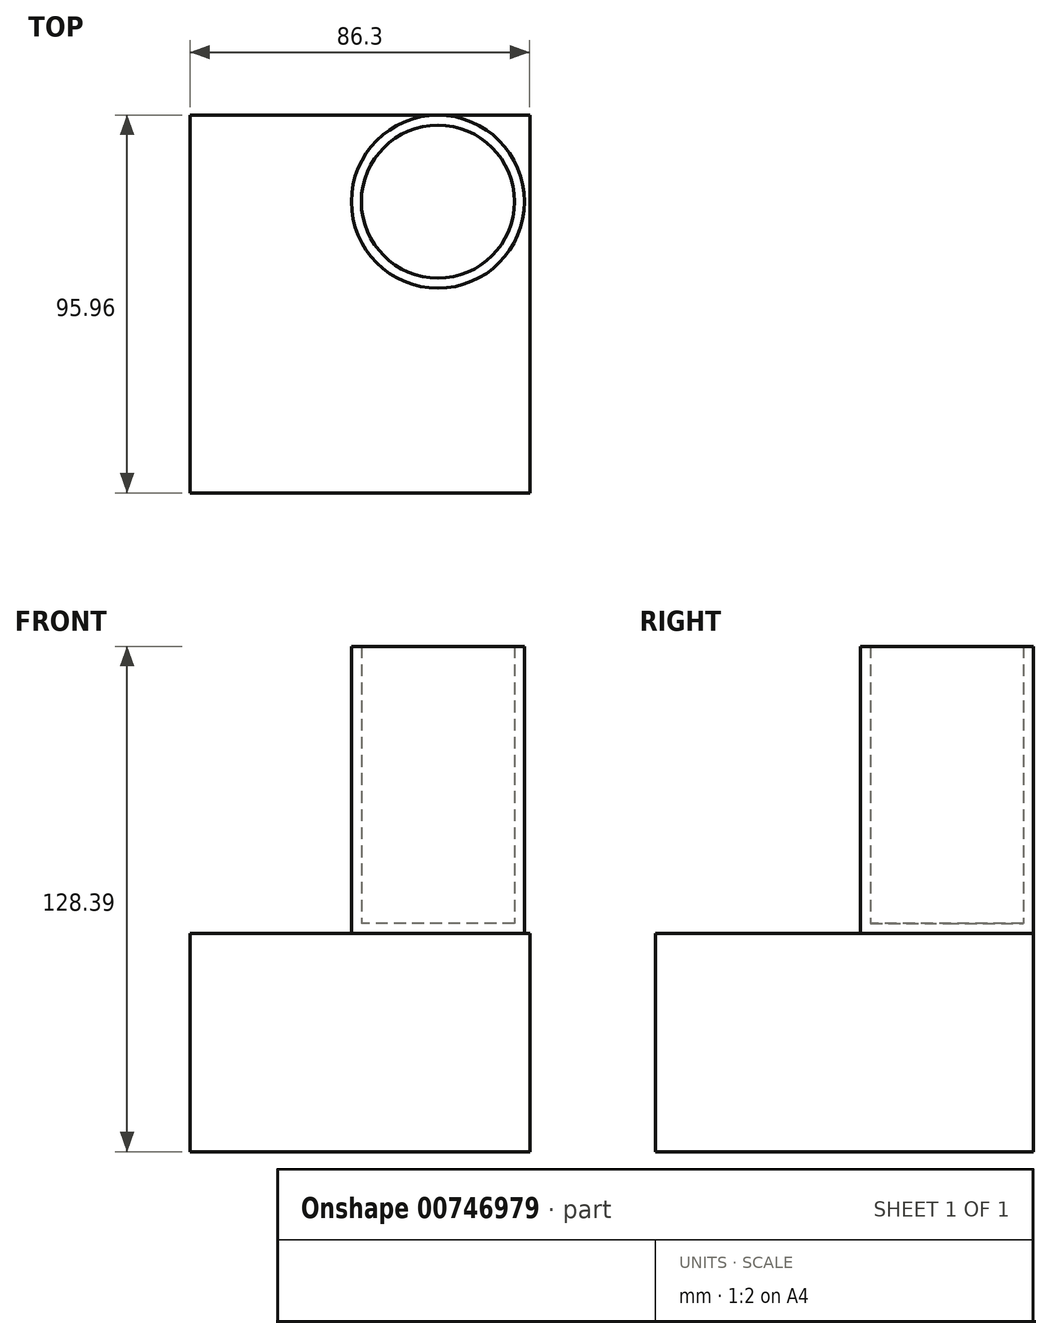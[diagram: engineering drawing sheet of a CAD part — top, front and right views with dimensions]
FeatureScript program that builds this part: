
annotation { "Feature Type Name" : "Feature", "Feature Type Description" : "" }
export const myFeature = defineFeature(function(context is Context, id is Id, definition is map)
    precondition{}
    {
        {
            var Q0;
            Q0=qCreatedBy(makeId("Top.planeOp"),FACE);
            var sketch = newSketch(context, id + "F0", { "sketchPlane" : qUnion([Q0])});
            skLineSegment(sketch, "E0.bottom", {"start": v(-43.15, -47.98) * mm, "end": v(43.15, -47.98) * mm});
            skLineSegment(sketch, "E0.top", {"start": v(-43.15, 47.98) * mm, "end": v(43.15, 47.98) * mm});
            skLineSegment(sketch, "E0.left", {"start": v(-43.15, -47.98) * mm, "end": v(-43.15, 47.98) * mm});
            skLineSegment(sketch, "E0.right", {"start": v(43.15, -47.98) * mm, "end": v(43.15, 47.98) * mm});
            skPoint(sketch, "E0.middle", {"position": v(0, 0) * mm});
            skSolve(sketch);
        }
        {
            var Q0;
            Q0=makeQuery(id+"F0.imprint","IMPRINT",FACE,{"disambiguationData":[TD([[makeQuery(id+"F0.imprint","IMPRINT",EDGE,{"derivedFrom":sQuery(id+"F0.wireOp",EDGE,"E0.bottom")}),1.0]])]});
            var sketch = newSketch(context, id + "F1", { "sketchPlane" : qUnion([Q0])});
            skSolve(sketch);
        }
        {
            var Q0;
            Q0=makeQuery(id+"F1.imprint","IMPRINT",FACE,{"disambiguationData":[TD([[makeQuery(id+"F1.imprint","IMPRINT",EDGE,{"derivedFrom":makeQuery(id+"F0.imprint","IMPRINT",EDGE,{"derivedFrom":sQuery(id+"F0.wireOp",EDGE,"E0.bottom")})}),1.0]])]});
            extrude(context, id + "F2", {"entities" : qUnion([Q0]), "depth" : 55.5 * mm, "offsetDistance" : 25.4 * mm});
        }
        {
            var Q0;
            Q0=makeQuery(id+"F2.opExtrude","CAP_FACE",FACE,{"disambiguationData":[OSD([sQuery(id+"F0.wireOp",EDGE,"E0.bottom"),sQuery(id+"F0.wireOp",EDGE,"E0.top"),sQuery(id+"F0.wireOp",EDGE,"E0.left"),sQuery(id+"F0.wireOp",EDGE,"E0.right")])],"isStart":false});
            var sketch = newSketch(context, id + "F3", { "sketchPlane" : qUnion([Q0])});
            skCircle(sketch, "E1", {"center": v(19.82, 26) * mm, "radius": 21.98 * mm});
            skSolve(sketch);
        }
        {
            var Q0;
            Q0=makeQuery(id+"F3.imprint","IMPRINT",FACE,{"disambiguationData":[TD([[makeQuery(id+"F3.imprint","IMPRINT",EDGE,{"derivedFrom":sQuery(id+"F3.wireOp",EDGE,"E1")}),1.0]])]});
            var Q1;
            Q1=sQuery(id+"F3.wireOp",EDGE,"E1");
            extrude(context, id + "F4", {"entities" : qUnion([Q0]), "surfaceEntities" : qUnion([Q1]), "depth" : 72.9 * mm, "offsetDistance" : 25.4 * mm});
        }
        {
            var Q0;
            Q0=makeQuery(id+"F4.opExtrude","CAP_FACE",FACE,{"disambiguationData":[OSD([sQuery(id+"F3.wireOp",EDGE,"E1")])],"isStart":false});
            shell(context, id + "F5", {"entities" : qUnion([Q0]), "thickness" : 2.54 * mm});
        }
    });
